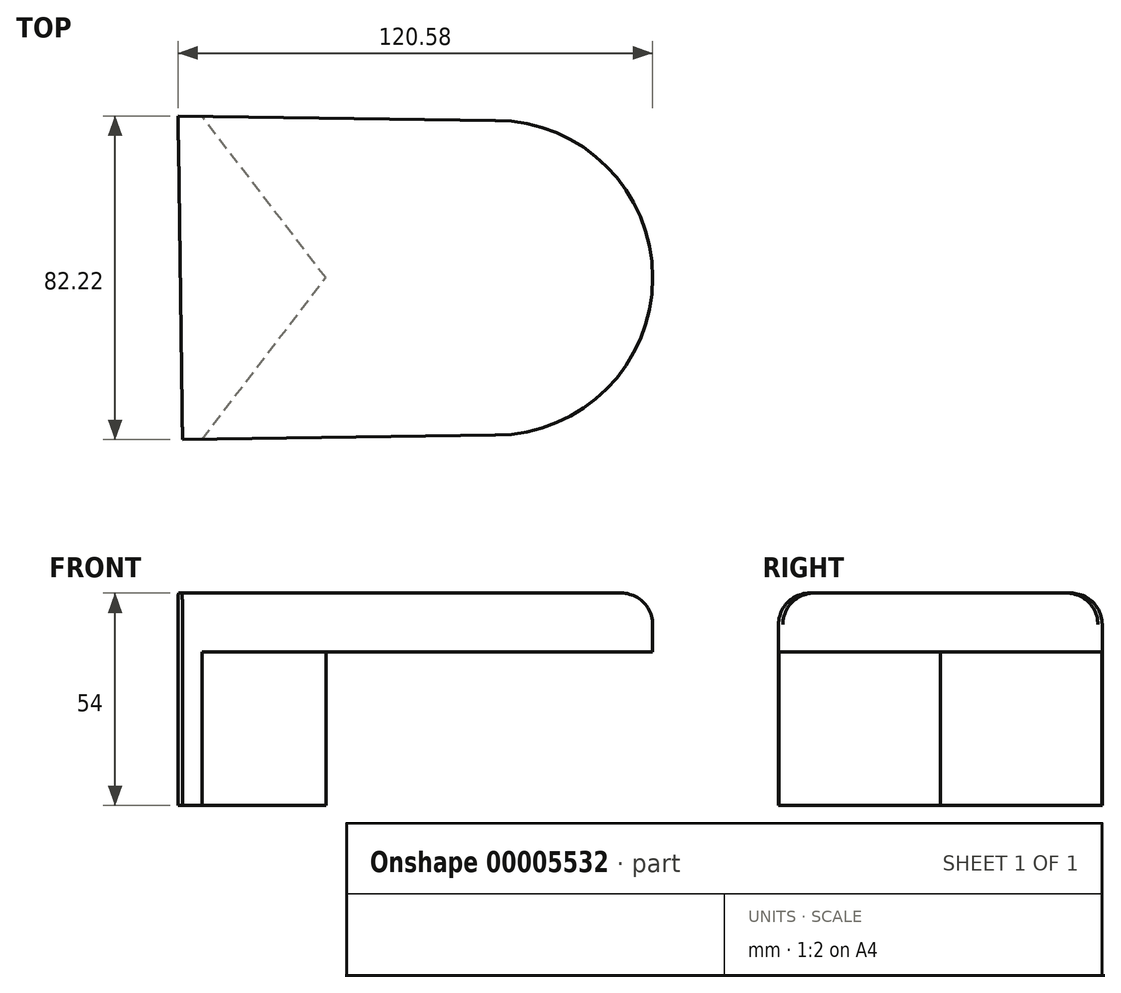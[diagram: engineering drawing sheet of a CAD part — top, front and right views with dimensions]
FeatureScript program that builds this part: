
annotation { "Feature Type Name" : "Feature", "Feature Type Description" : "" }
export const myFeature = defineFeature(function(context is Context, id is Id, definition is map)
    precondition{}
    {
        {
            var Q0;
            Q0=qCreatedBy(makeId("Top.planeOp"),FACE);
            var sketch = newSketch(context, id + "F0", { "sketchPlane" : qUnion([Q0])});
            skArc(sketch, "E0", {"start": v(0, -40) * mm, "mid": v(40, 0) * mm, "end": v(0, 40) * mm});
            skLineSegment(sketch, "E1", {"start": v(-80.58, 41.12) * mm, "end": v(0, 40) * mm});
            skLineSegment(sketch, "E2", {"start": v(0, -40) * mm, "end": v(-79.44, -41.1) * mm});
            skLineSegment(sketch, "E3", {"start": v(-79.44, -41.1) * mm, "end": v(-80.58, 41.12) * mm});
            skSolve(sketch);
        }
        {
            var Q0;
            Q0=makeQuery(id+"F0.imprint","IMPRINT",FACE,{"disambiguationData":[TD([[makeQuery(id+"F0.imprint","IMPRINT",EDGE,{"derivedFrom":sQuery(id+"F0.wireOp",EDGE,"E0")}),1.0]])]});
            extrude(context, id + "F1", {"entities" : qUnion([Q0]), "depth" : 54 * mm});
        }
        {
            var Q0;
            Q0=makeQuery(id+"F1.opExtrude","SWEPT_EDGE",EDGE,{"disambiguationData":[OSD([sQuery(id+"F0.wireOp",EDGE,"E0"),sQuery(id+"F0.wireOp",EDGE,"E2")])]});
            var Q1;
            Q1=makeQuery(id+"F1.opExtrude","SWEPT_EDGE",EDGE,{"disambiguationData":[OSD([sQuery(id+"F0.wireOp",EDGE,"E0"),sQuery(id+"F0.wireOp",EDGE,"E1")])]});
            fillet(context, id + "F2", {"entities" : qUnion([Q0, Q1]), "radius" : 15 * mm, "tangentPropagation" : true, "allowEdgeOverflow" : false});
        }
        {
            var Q0;
            Q0=makeQuery(id+"F1.opExtrude","CAP_FACE",FACE,{"disambiguationData":[OSD([sQuery(id+"F0.wireOp",EDGE,"E0"),sQuery(id+"F0.wireOp",EDGE,"E1"),sQuery(id+"F0.wireOp",EDGE,"E2"),sQuery(id+"F0.wireOp",EDGE,"E3")])],"isStart":true});
            var sketch = newSketch(context, id + "F3", { "sketchPlane" : qUnion([Q0])});
            skLineSegment(sketch, "E4", {"start": v(-74.44, 41.03) * mm, "end": v(-43, 0) * mm});
            skLineSegment(sketch, "E5", {"start": v(-43, 0) * mm, "end": v(-74.44, -41.03) * mm});
            skLineSegment(sketch, "E6", {"start": v(-74.44, 41.03) * mm, "end": v(47.2, 55.89) * mm});
            skLineSegment(sketch, "E7", {"start": v(47.2, 55.89) * mm, "end": v(48.63, -68.12) * mm});
            skLineSegment(sketch, "E8", {"start": v(48.63, -68.12) * mm, "end": v(-74.44, -41.03) * mm});
            skSolve(sketch);
        }
        {
            var Q0;
            {var subQ2=sQuery(id+"F3.wireOp",EDGE,"E4");var subQ3=sQuery(id+"F3.wireOp",EDGE,"E6");Q0=qUnion([makeQuery(id+"F3.imprint","IMPRINT",FACE,{"disambiguationData":[TD([[makeQuery(id+"F3.imprint","IMPRINT",EDGE,{"derivedFrom":subQ3}),-1.0]])]}),makeQuery(id+"F3.imprint","IMPRINT",FACE,{"disambiguationData":[TD([[makeQuery(id+"F3.imprint","IMPRINT",EDGE,{"derivedFrom":subQ2}),1.0]])]})]);}
            extrude(context, id + "F4", {"entities" : qUnion([Q0]), "operationType" : NewBodyOperationType.REMOVE, "oppositeDirection" : true, "depth" : 39 * mm});
        }
        {
            var Q0;
            Q0=makeQuery(id+"F4.boolean.opBoolean","COPY",EDGE,{"derivedFrom":makeQuery(id+"F4.opExtrude","CAP_EDGE",EDGE,{"disambiguationData":[OSD([sQuery(id+"F3.wireOp",EDGE,"E4")])],"isStart":true})});
            var Q1;
            Q1=makeQuery(id+"F4.boolean.opBoolean","COPY",EDGE,{"derivedFrom":makeQuery(id+"F4.opExtrude","CAP_EDGE",EDGE,{"disambiguationData":[OSD([sQuery(id+"F3.wireOp",EDGE,"E5")])],"isStart":true})});
            var Q2;
            Q2=makeQuery(id+"F1.opExtrude","CAP_EDGE",EDGE,{"disambiguationData":[OSD([sQuery(id+"F0.wireOp",EDGE,"E2")])],"isStart":false});
            fillet(context, id + "F5", {"entities" : qUnion([Q0, Q1, Q2]), "radius" : 8 * mm, "tangentPropagation" : true, "allowEdgeOverflow" : false});
        }
    });
